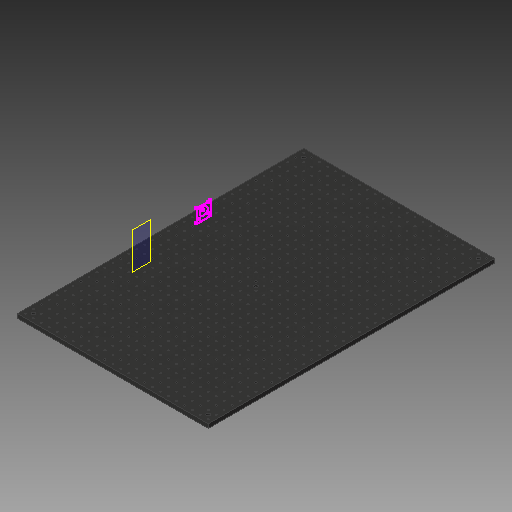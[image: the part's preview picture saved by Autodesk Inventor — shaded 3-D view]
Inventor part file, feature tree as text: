
AUTODESK INVENTOR PART (.ipt)
format: ipt  version: 2017 (Build 210142000, 142)  size: 1,197,568 bytes
history: native  units: in
note: dims shown in document units (in); Inventor stores cm internally (conversion verified against a paired STEP export)
features: other x4, sketch x2, plane x1, reference x1
ambient origin geometry x8: Origin, YZ Plane, XZ Plane, XY Plane, X Axis, Y Axis, Z Axis, Center Point
bodies: Solid1 (feature_tree)
feature tree (8):
  plane  "Work Plane1"
  sketch  "Sketch1"
  sketch  "Sketch2"
  reference  "Reference1"
  other  "13808-001-1-solid1"
  parser-record x1  (decoder bookkeeping rows leaked as tree rows — omitted from the tree; the rows remain in map.json)
  other  "ZT_Main_Assembly.iam"
  other  "DFM_M-Solidworks:3"
note: 1 file-system path scrubbed to <path> (originals preserved in map.json)
